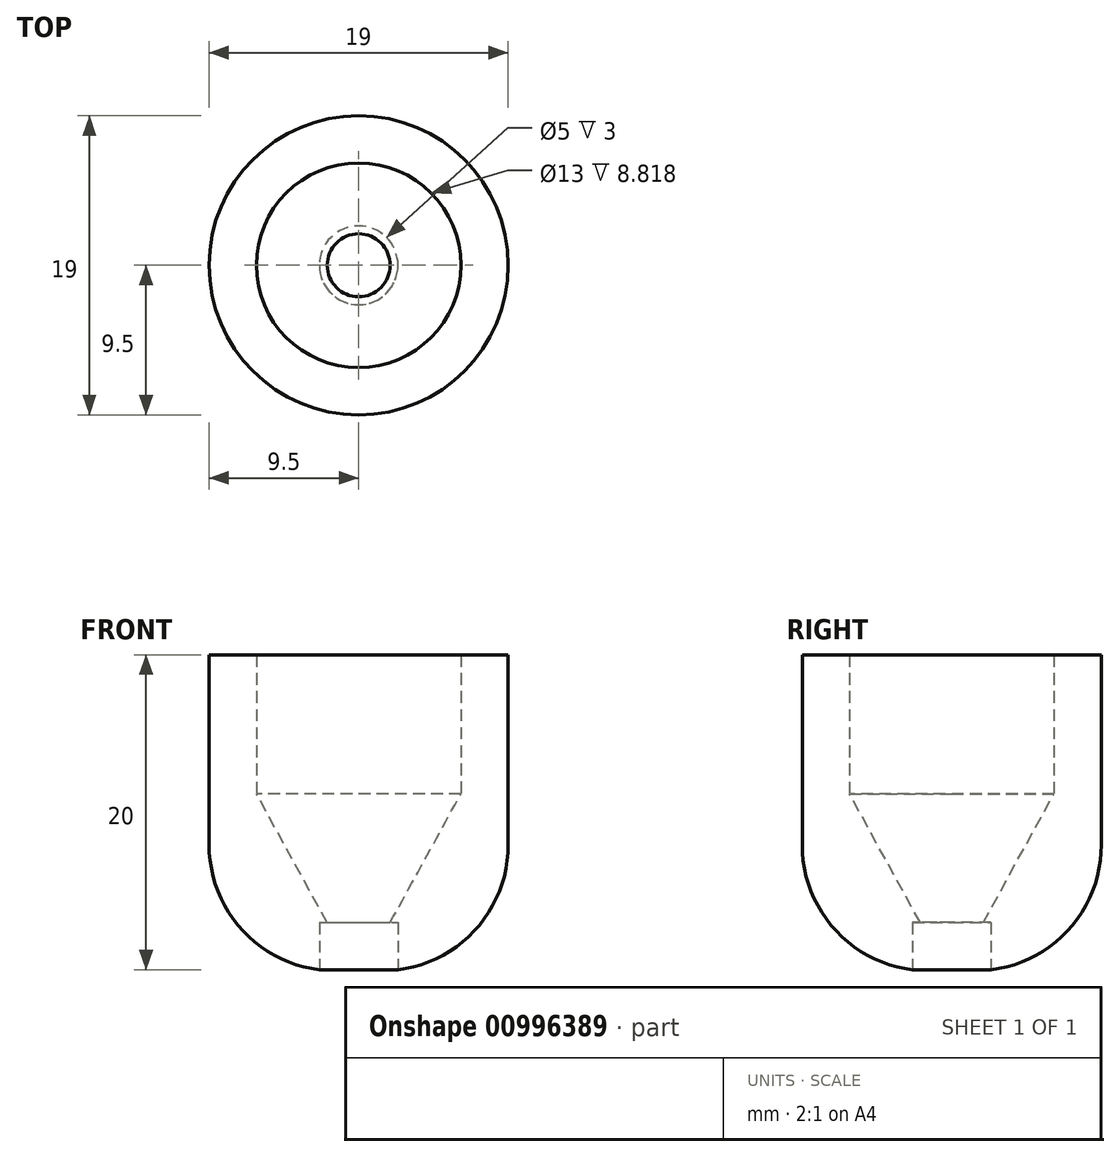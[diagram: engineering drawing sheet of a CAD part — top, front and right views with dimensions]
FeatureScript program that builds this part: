
annotation { "Feature Type Name" : "Feature", "Feature Type Description" : "" }
export const myFeature = defineFeature(function(context is Context, id is Id, definition is map)
    precondition{}
    {
        {
            var Q0;
            Q0=qCreatedBy(makeId("Top.planeOp"),FACE);
            var sketch = newSketch(context, id + "F0", { "sketchPlane" : qUnion([Q0])});
            skCircle(sketch, "E0", {"center": v(0, 0) * mm, "radius": 6.5 * mm});
            skCircle(sketch, "E1.0", {"center": v(0, 0) * mm, "radius": 9.5 * mm});
            skCircle(sketch, "E2", {"center": v(0, 0) * mm, "radius": 2.5 * mm});
            skSolve(sketch);
        }
        {
            var Q0;
            Q0=makeQuery(id+"F0.imprint","IMPRINT",FACE,{"disambiguationData":[TD([[makeQuery(id+"F0.imprint","IMPRINT",EDGE,{"derivedFrom":sQuery(id+"F0.wireOp",EDGE,"E0")}),1.0]])]});
            extrude(context, id + "F1", {"entities" : qUnion([Q0]), "depth" : 3 * mm, "offsetDistance" : 25 * mm});
        }
        {
            var Q0;
            Q0=makeQuery(id+"F0.imprint","IMPRINT",FACE,{"disambiguationData":[TD([[makeQuery(id+"F0.imprint","IMPRINT",EDGE,{"derivedFrom":sQuery(id+"F0.wireOp",EDGE,"E0")}),-1.0]])]});
            extrude(context, id + "F2", {"entities" : qUnion([Q0]), "operationType" : NewBodyOperationType.ADD, "depth" : 20 * mm, "offsetDistance" : 25 * mm});
        }
        {
            var Q0;
            Q0=makeQuery(id+"F2.opExtrude","CAP_EDGE",EDGE,{"disambiguationData":[OSD([sQuery(id+"F0.wireOp",EDGE,"E1.0")])],"isStart":true});
            fillet(context, id + "F3", {"entities" : qUnion([Q0]), "radius" : 8 * mm, "tangentPropagation" : true, "allowEdgeOverflow" : false});
        }
        {
            var Q0;
            Q0=qCreatedBy(makeId("Right.planeOp"),FACE);
            var sketch = newSketch(context, id + "F4", { "sketchPlane" : qUnion([Q0])});
            skLineSegment(sketch, "E3", {"start": v(0, 0) * mm, "end": v(0, 3) * mm});
            skLineSegment(sketch, "E4", {"start": v(0, 3) * mm, "end": v(2, 3) * mm});
            skLineSegment(sketch, "E5", {"start": v(2, 3) * mm, "end": v(7.5, 3) * mm});
            skLineSegment(sketch, "E6", {"start": v(7.5, 3) * mm, "end": v(7.5, 13) * mm});
            skLineSegment(sketch, "E7", {"start": v(7.5, 13) * mm, "end": v(2, 3) * mm});
            skSolve(sketch);
        }
        {
            var Q0;
            Q0=makeQuery(id+"F4.imprint","IMPRINT",FACE,{"disambiguationData":[TD([[makeQuery(id+"F4.imprint","IMPRINT",EDGE,{"derivedFrom":sQuery(id+"F4.wireOp",EDGE,"E5")}),1.0]])]});
            var Q1;
            Q1=sQuery(id+"F4.wireOp",EDGE,"E3");
            revolve(context, id + "F5", {"operationType" : NewBodyOperationType.ADD, "surfaceOperationType" : NewSurfaceOperationType.NEW, "entities" : qUnion([Q0]), "axis" : qUnion([Q1]), "revolveType" : RevolveType.FULL});
        }
    });
